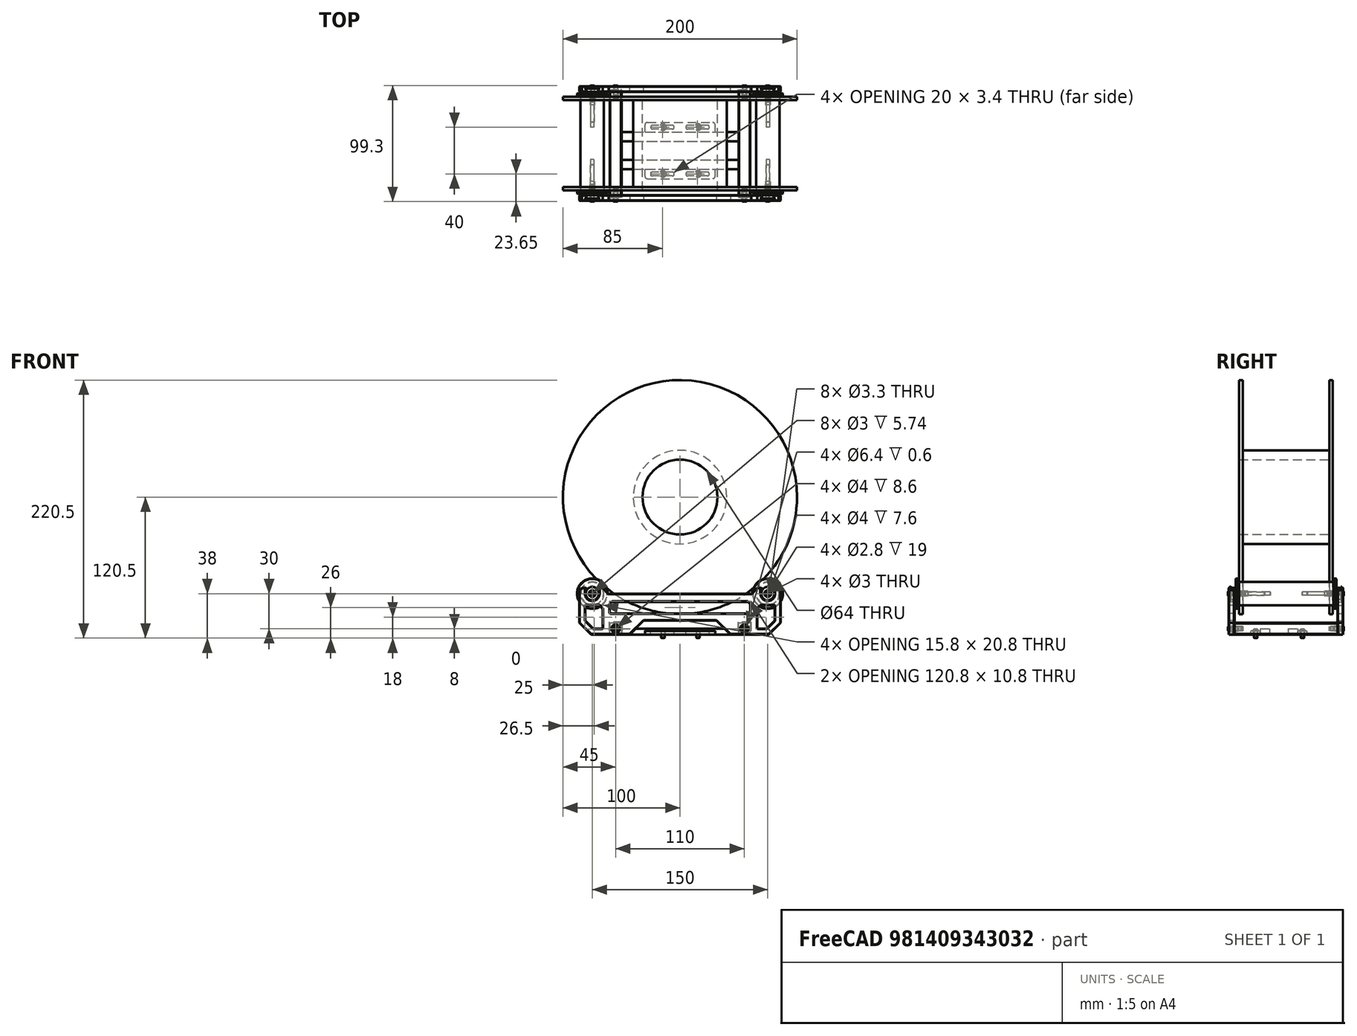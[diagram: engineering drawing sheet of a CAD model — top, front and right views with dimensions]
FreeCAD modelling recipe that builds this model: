
FCSTD DOCUMENT  (FreeCAD 0.19R24291 (Git))
Label: spool-holder-assembly
License: Other
LicenseURL: GPL3
objects: Part::FeaturePython×20, Part::Feature×14, PartDesign::CoordinateSystem×1, App::Part×1
note: 35 computed .brp shape members not serialized (recipe doc carries the construction recipe); baked Part::Feature solids carry a one-line shape summary decoded from their .brp

FEATURE [Part::Feature] Cut008004003004014002002005003004003002003021022001002001105001001  label="F623-bearing002"
  Placement = pos=(-75,-48,35) rot=(-1,0,0;1.5708rad)
  shape: bbox 11.5 x 4 x 11.5 mm, 6 faces (baked)
FEATURE [Part::Feature] Chamfer004013007011015006009007001083001004  label="spool-holder-spacer003"
  Placement = pos=(75,-41,35) rot=(1,0,0;1.5708rad)
  shape: bbox 26 x 3 x 26 mm, 9 faces (baked)
FEATURE [Part::Feature] Cut008004003004014002002005003004003002003021022001002001105001003  label="F623-bearing004"
  Placement = pos=(75,48,35) rot=(0,0.707107,-0.707107;3.14159rad)
  shape: bbox 11.5 x 4 x 11.5 mm, 6 faces (baked)
FEATURE [Part::Feature] Cut002002002002006  label="filament-spoll"
  Placement = pos=(0,-40,117.5) rot=(-1,0,0;1.5708rad)
  shape: bbox 200 x 80 x 200 mm, 8 faces (baked)
FEATURE [Part::FeaturePython] Screw1344  label="M3x30-Screw002"  # Fasteners workbench fastener (typed FeaturePython)
  Placement = pos=(75,48,35) rot=(-1,0,0;1.5708rad)
  baseObject = -> Cut008004003004014002002005003004003002003021022001002001105001003 [Edge9]
  diameter = 1
  invert = true
  length = 8
  lengthCustom = 30
  matchOuter = true
  offset = 0
  thread = false
  type = 39
FEATURE [Part::Feature] Chamfer004013007011015006009007001082001002  label="spool-holder-face001"
  Placement = pos=(0,1,0) rot=(0,0,1;3.14159rad)
  shape: bbox 172 x 5 x 40 mm, 230 faces (baked)
FEATURE [Part::FeaturePython] Screw1345  label="M3x6-Screw100"  # Fasteners workbench fastener (typed FeaturePython)
  Placement = pos=(-14.6,-25.9,3) rot=(0,0,1;0rad)
  diameter = 1
  invert = false
  length = 0
  lengthCustom = 6
  matchOuter = true
  offset = 0
  thread = false
  type = 39
FEATURE [Part::Feature] Cut008004003004014002002005003004003002003021022001002001105001002  label="F623-bearing003"
  Placement = pos=(75,-48,35) rot=(-1,0,0;1.5708rad)
  shape: bbox 11.5 x 4 x 11.5 mm, 6 faces (baked)
FEATURE [Part::FeaturePython] Screw1346  label="M3x10-Screw181"  # Fasteners workbench fastener (typed FeaturePython)
  Placement = pos=(-55,-48,5) rot=(1,0,0;1.5708rad)
  baseObject = -> Chamfer004013007011015006009007001082001002 [Edge534]
  diameter = 1
  invert = true
  length = 2
  lengthCustom = 10
  matchOuter = true
  offset = 0
  thread = false
  type = 39
FEATURE [Part::Feature] Chamfer004013007011015006009007001083001005  label="spool-holder-roller"
  Placement = pos=(75,41,35) rot=(1,0,0;1.5708rad)
  shape: bbox 20 x 81.5 x 20 mm, 15 faces (baked)
FEATURE [Part::FeaturePython] Screw1347  label="M3x30-Screw"  # Fasteners workbench fastener (typed FeaturePython)
  Placement = pos=(-75,-48,35) rot=(1,0,0;1.5708rad)
  baseObject = -> Cut008004003004014002002005003004003002003021022001002001105001001 [Edge9]
  diameter = 1
  invert = true
  length = 8
  lengthCustom = 30
  matchOuter = true
  offset = 0
  thread = false
  type = 39
FEATURE [Part::Feature] Chamfer004013007011015006009007001005003007001016  label="spool-holder-base"
  shape: bbox 120 x 92 x 10 mm, 79 faces (baked)
FEATURE [Part::Feature] Cut008004003004014002002005003004003002003021022001002001105001004  label="F623-bearing005"
  Placement = pos=(-75,48,35) rot=(0,0.707107,-0.707107;3.14159rad)
  shape: bbox 11.5 x 4 x 11.5 mm, 6 faces (baked)
FEATURE [Part::FeaturePython] Screw1343  label="M3x30-Screw003"  # Fasteners workbench fastener (typed FeaturePython)
  Placement = pos=(-75,48,35) rot=(-1,0,0;1.5708rad)
  baseObject = -> Cut008004003004014002002005003004003002003021022001002001105001004 [Edge9]
  diameter = 1
  invert = true
  length = 8
  lengthCustom = 30
  matchOuter = true
  offset = 0
  thread = false
  type = 39
FEATURE [Part::FeaturePython] Screw1348  label="M3x6-Screw101"  # Fasteners workbench fastener (typed FeaturePython)
  Placement = pos=(15.4,14.1,3) rot=(0,0,1;0rad)
  diameter = 1
  invert = false
  length = 0
  lengthCustom = 6
  matchOuter = true
  offset = 0
  thread = false
  type = 39
FEATURE [Part::Feature] Chamfer004013007011015006009007001083001003  label="spool-holder-spacer002"
  Placement = pos=(75,41,35) rot=(0,0.707107,0.707107;3.14159rad)
  shape: bbox 26 x 3 x 26 mm, 9 faces (baked)
FEATURE [Part::Feature] Chamfer004013007011015006009007001084001  label="spool-holder-roller001"
  Placement = pos=(-75,41,35) rot=(1,0,0;1.5708rad)
  shape: bbox 20 x 81.5 x 20 mm, 15 faces (baked)
FEATURE [Part::Feature] Chamfer004013007011015006009007001083001002  label="spool-holder-spacer001"
  Placement = pos=(-75,41,35) rot=(0,0.707107,0.707107;3.14159rad)
  shape: bbox 26 x 3 x 26 mm, 9 faces (baked)
FEATURE [Part::FeaturePython] Screw1349  label="M3x6-Screw102"  # Fasteners workbench fastener (typed FeaturePython)
  Placement = pos=(-14.6,14.1,3) rot=(0,0,1;0rad)
  diameter = 1
  invert = false
  length = 0
  lengthCustom = 6
  matchOuter = true
  offset = 0
  thread = false
  type = 39
FEATURE [Part::FeaturePython] Screw1350  label="M3x10-Screw182"  # Fasteners workbench fastener (typed FeaturePython)
  Placement = pos=(55,-48,5) rot=(1,0,0;1.5708rad)
  baseObject = -> Chamfer004013007011015006009007001082001002 [Edge533]
  diameter = 1
  invert = true
  length = 2
  lengthCustom = 10
  matchOuter = true
  offset = 0
  thread = false
  type = 39
FEATURE [Part::Feature] Chamfer004013007011015006009007001083001001  label="spool-holder-spacer"
  Placement = pos=(-75,-41,35) rot=(1,0,0;1.5708rad)
  shape: bbox 26 x 3 x 26 mm, 9 faces (baked)
FEATURE [Part::FeaturePython] Screw1351  label="M3x6-Screw103"  # Fasteners workbench fastener (typed FeaturePython)
  Placement = pos=(15.4,-25.9,3) rot=(0,0,1;0rad)
  diameter = 1
  invert = false
  length = 0
  lengthCustom = 6
  matchOuter = true
  offset = 0
  thread = false
  type = 39
FEATURE [Part::Feature] Chamfer004013007011015006009007001081001001  label="spool-holder-face"
  Placement = pos=(0,-1,0) rot=(0,0,1;0rad)
  shape: bbox 172 x 5 x 40 mm, 230 faces (baked)
FEATURE [Part::FeaturePython] Screw1341  label="M3x10-Screw179"  # Fasteners workbench fastener (typed FeaturePython)
  Placement = pos=(55,48,5) rot=(-1,0,0;1.5708rad)
  baseObject = -> Chamfer004013007011015006009007001081001001 [Edge534]
  diameter = 1
  invert = true
  length = 2
  lengthCustom = 10
  matchOuter = true
  offset = 0
  thread = false
  type = 39
FEATURE [Part::FeaturePython] Screw1342  label="M3x10-Screw180"  # Fasteners workbench fastener (typed FeaturePython)
  Placement = pos=(-55,48,5) rot=(-1,0,0;1.5708rad)
  baseObject = -> Chamfer004013007011015006009007001081001001 [Edge533]
  diameter = 1
  invert = true
  length = 2
  lengthCustom = 10
  matchOuter = true
  offset = 0
  thread = false
  type = 39
FEATURE [Part::FeaturePython] Screw1352  label="M3x30-Screw001"  # Fasteners workbench fastener (typed FeaturePython)
  Placement = pos=(75,-48,35) rot=(1,0,0;1.5708rad)
  baseObject = -> Cut008004003004014002002005003004003002003021022001002001105001002 [Edge9]
  diameter = 1
  invert = true
  length = 8
  lengthCustom = 30
  matchOuter = true
  offset = 0
  thread = false
  type = 39
FEATURE [Part::FeaturePython] HeatSet  label="M3x4-HeatSet"  # WARN: FeaturePython — macro-defined, semantics opaque (R4)
  Placement = pos=(75,41,35) rot=(-1,0,0;1.5708rad)
  baseObject = -> Chamfer004013007011015006009007001083001005 [Edge8]
  diameter = 2
  invert = true
  offset = 0
FEATURE [Part::FeaturePython] HeatSet001  label="M3x4-HeatSet001"  # WARN: FeaturePython — macro-defined, semantics opaque (R4)
  Placement = pos=(55,46,5) rot=(-1,0,0;1.5708rad)
  baseObject = -> Chamfer004013007011015006009007001005003007001016 [Edge124]
  diameter = 2
  invert = true
  offset = 0
FEATURE [Part::FeaturePython] HeatSet002  label="M3x4-HeatSet002"  # WARN: FeaturePython — macro-defined, semantics opaque (R4)
  Placement = pos=(-55,46,5) rot=(-1,0,0;1.5708rad)
  baseObject = -> Chamfer004013007011015006009007001005003007001016 [Edge8]
  diameter = 2
  invert = true
  offset = 0
FEATURE [Part::FeaturePython] HeatSet003  label="M3x4-HeatSet003"  # WARN: FeaturePython — macro-defined, semantics opaque (R4)
  Placement = pos=(-75,41,35) rot=(-1,0,0;1.5708rad)
  baseObject = -> Chamfer004013007011015006009007001084001 [Edge8]
  diameter = 2
  invert = true
  offset = 0
FEATURE [Part::FeaturePython] HeatSet005  label="M3x4-HeatSet004"  # WARN: FeaturePython — macro-defined, semantics opaque (R4)
  Placement = pos=(75,-40.5,35) rot=(1,0,0;1.5708rad)
  baseObject = -> Chamfer004013007011015006009007001083001005 [Edge9]
  diameter = 2
  invert = false
  offset = 0
FEATURE [Part::FeaturePython] HeatSet008  label="M3x4-HeatSet005"  # WARN: FeaturePython — macro-defined, semantics opaque (R4)
  Placement = pos=(-55,-46,5) rot=(1,0,0;1.5708rad)
  baseObject = -> Chamfer004013007011015006009007001005003007001016 [Edge28]
  diameter = 2
  invert = false
  offset = 0
FEATURE [Part::FeaturePython] HeatSet009  label="M3x4-HeatSet006"  # WARN: FeaturePython — macro-defined, semantics opaque (R4)
  Placement = pos=(55,-46,5) rot=(1,0,0;1.5708rad)
  baseObject = -> Chamfer004013007011015006009007001005003007001016 [Edge132]
  diameter = 2
  invert = false
  offset = 0
FEATURE [Part::FeaturePython] HeatSet011  label="M3x4-HeatSet007"  # WARN: FeaturePython — macro-defined, semantics opaque (R4)
  Placement = pos=(-75,-40.5,35) rot=(1,0,0;1.5708rad)
  baseObject = -> Chamfer004013007011015006009007001084001 [Edge9]
  diameter = 2
  invert = false
  offset = 0
FEATURE [PartDesign::CoordinateSystem] LCS_spool_holder  label="LCS_spool-holder"
  AttacherType = Attacher::AttachEngine3D
FEATURE [App::Part] Part196  label="spool-holder"
  Group = -> [Chamfer004013007011015006009007001005003007001016,Cut002002002002006,Screw1348,Screw1351,Screw1345,Screw1349,Screw1347,Cut008004003004014002002005003004003002003021022001002001105001001,Screw1341,Screw1342,Chamfer004013007011015006009007001081001001,Screw1346,Screw1350,Chamfer004013007011015006009007001082001002,Screw1352,Cut008004003004014002002005003004003002003021022001002001105001002,+19 more]
  Origin = -> Origin204
  Placement = pos=(0,0.5,0.5) rot=(0,0,1;0rad)
